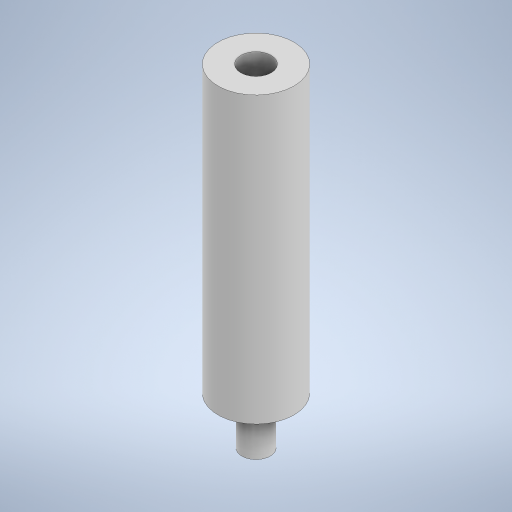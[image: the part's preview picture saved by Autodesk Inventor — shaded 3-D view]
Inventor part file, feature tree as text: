
AUTODESK INVENTOR PART (.ipt)
format: ipt  version: 2024.2 (Build 282272000, 272)  size: 236,544 bytes
history: native  units: mm
features: extrude x3, sketch x3
ambient origin geometry x8: Origin, YZ Plane, XZ Plane, XY Plane, X Axis, Y Axis, Z Axis, Center Point
bodies: Solid1 (feature_tree)
feature tree (6):
  extrude  "Extrusion1"  Depth=5.0mm TaperAngle=0.0deg
  extrude  "Extrusion2"  Depth=30.0mm TaperAngle=0.0deg
  extrude  "Extrusion3"  Depth=2.5mm TaperAngle=0.0deg
  sketch  "Sketch1"  dims[d0=3.0mm d1=5.0mm d2=0.0mm]
  sketch  "Sketch2"  dims[d3=8.0mm d4=30.0mm d5=0.0mm]
  sketch  "Sketch3"  dims[d6=3.2mm d7=2.5mm d8=0.0mm]
